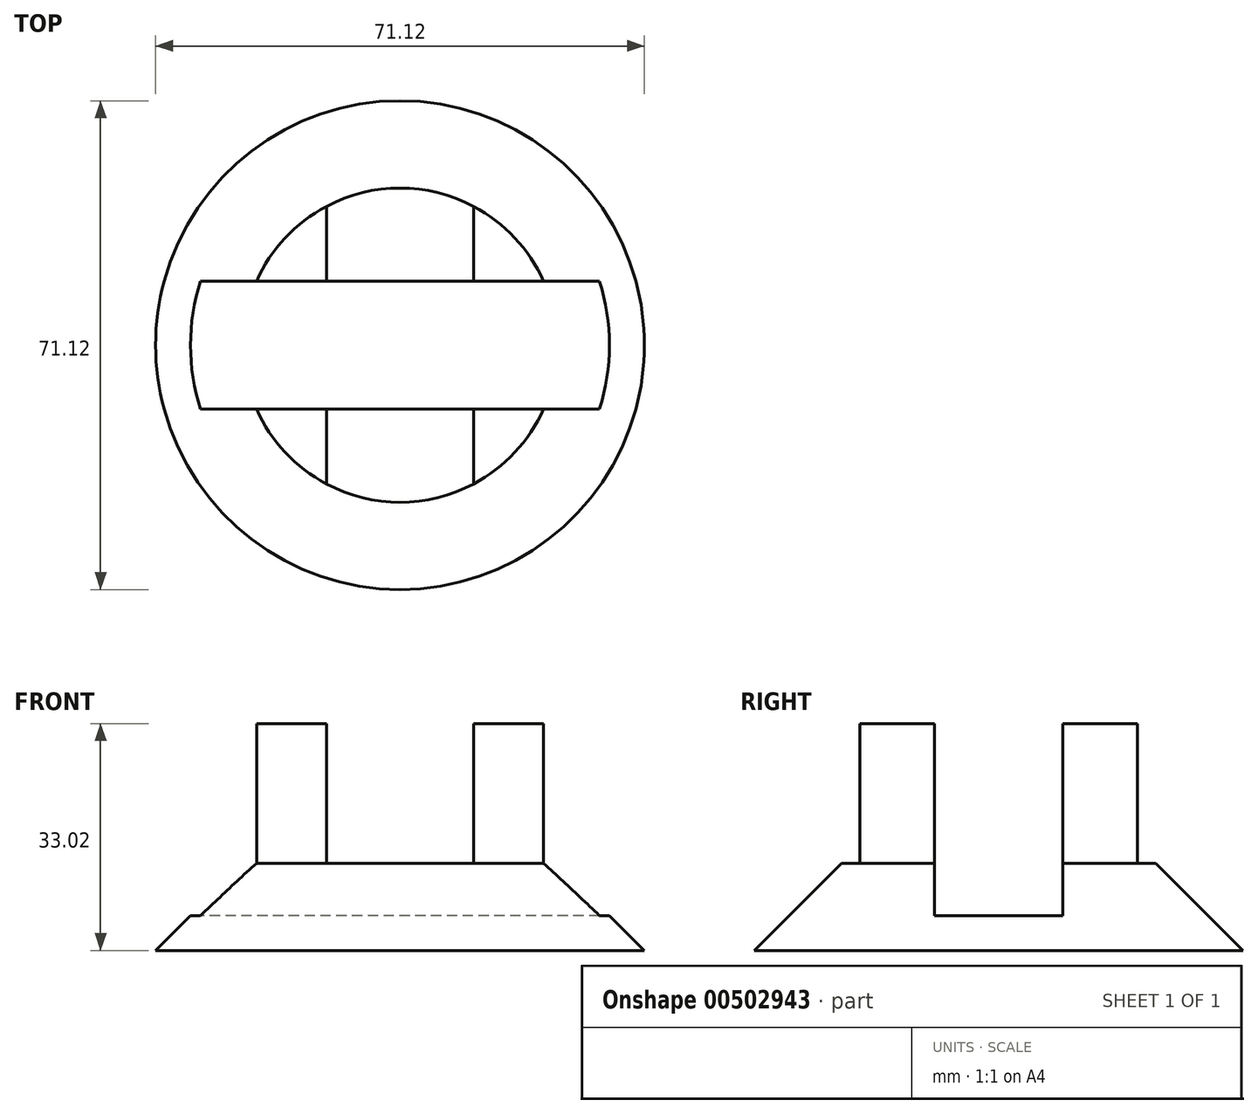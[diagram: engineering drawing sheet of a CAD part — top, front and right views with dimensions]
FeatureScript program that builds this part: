
annotation { "Feature Type Name" : "Feature", "Feature Type Description" : "" }
export const myFeature = defineFeature(function(context is Context, id is Id, definition is map)
    precondition{}
    {
        {
            var Q0;
            Q0=qCreatedBy(makeId("Top.planeOp"),FACE);
            var sketch = newSketch(context, id + "F0", { "sketchPlane" : qUnion([Q0])});
            skCircle(sketch, "E0", {"center": v(0, 0) * mm, "radius": 35.56 * mm});
            skLineSegment(sketch, "E1", {"start": v(34.32, -9.32) * mm, "end": v(-34.32, -9.32) * mm});
            skLineSegment(sketch, "E2", {"start": v(34.32, 9.32) * mm, "end": v(-34.32, 9.32) * mm});
            skSolve(sketch);
        }
        {
            var Q0;
            {var subQ2=sQuery(id+"F0.wireOp",EDGE,"E1");Q0=makeQuery(id+"F0.imprint","IMPRINT",FACE,{"disambiguationData":[TD([[makeQuery(id+"F0.imprint","IMPRINT",EDGE,{"derivedFrom":subQ2}),-1.0]])]});}
            extrude(context, id + "F1", {"entities" : qUnion([Q0]), "depth" : 5.08 * mm, "offsetDistance" : 25.4 * mm});
        }
        {
            var Q0;
            {var subQ0=sQuery(id+"F0.wireOp",EDGE,"E0");var subQ1=makeQuery(id+"F0.imprint","IMPRINT",VERTEX,{"derivedFrom":subQ0});Q0=makeQuery(id+"F1.opExtrude","CAP_EDGE",EDGE,{"disambiguationData":[OSD([subQ0]),TDD([makeQuery(id+"F0.imprint","IMPRINT",EDGE,{"disambiguationData":[TD([[subQ1,-1.0]])],"derivedFrom":subQ0}),makeQuery(id+"F0.imprint","IMPRINT",EDGE,{"disambiguationData":[TD([[subQ1,1.0]])],"derivedFrom":subQ0})])],"isStart":false});}
            var Q1;
            {var subQ0=sQuery(id+"F0.wireOp",EDGE,"E0");Q1=makeQuery(id+"F1.opExtrude","CAP_EDGE",EDGE,{"disambiguationData":[OSD([subQ0]),TDD([makeQuery(id+"F0.imprint","IMPRINT",EDGE,{"disambiguationData":[TD([[makeQuery(id+"F0.imprint","INTERSECT",VERTEX,{"disambiguationData":[OD(1.0)],"derivedFrom":[subQ0,sQuery(id+"F0.wireOp",EDGE,"E1")]}),1.0]])],"derivedFrom":subQ0})])],"isStart":false});}
            var Q2;
            {var subQ0=sQuery(id+"F0.wireOp",EDGE,"E0");Q2=makeQuery(id+"F1.opExtrude","CAP_EDGE",EDGE,{"disambiguationData":[OSD([subQ0]),TDD([makeQuery(id+"F0.imprint","IMPRINT",EDGE,{"disambiguationData":[TD([[makeQuery(id+"F0.imprint","INTERSECT",VERTEX,{"disambiguationData":[OD(0.0)],"derivedFrom":[subQ0,sQuery(id+"F0.wireOp",EDGE,"E1")]}),-1.0]])],"derivedFrom":subQ0})])],"isStart":false});}
            chamfer(context, id + "F2", {"entities" : qUnion([Q0, Q1, Q2]), "width" : 5.08 * mm, "tangentPropagation" : true});
        }
        {
            var Q0;
            {var subQ0=sQuery(id+"F0.wireOp",EDGE,"E1");Q0=makeQuery(id+"F0.imprint","IMPRINT",FACE,{"disambiguationData":[TD([[makeQuery(id+"F0.imprint","IMPRINT",EDGE,{"derivedFrom":subQ0}),1.0]])]});}
            extrude(context, id + "F3", {"entities" : qUnion([Q0]), "operationType" : NewBodyOperationType.ADD, "depth" : 12.7 * mm, "offsetDistance" : 25.4 * mm});
        }
        {
            var Q0;
            {var subQ0=sQuery(id+"F0.wireOp",EDGE,"E2");Q0=makeQuery(id+"F0.imprint","IMPRINT",FACE,{"disambiguationData":[TD([[makeQuery(id+"F0.imprint","IMPRINT",EDGE,{"derivedFrom":subQ0}),-1.0]])]});}
            extrude(context, id + "F4", {"entities" : qUnion([Q0]), "operationType" : NewBodyOperationType.ADD, "depth" : 12.7 * mm, "offsetDistance" : 25.4 * mm});
        }
        {
            var Q0;
            Q0=makeQuery(id+"F3.opExtrude","CAP_EDGE",EDGE,{"disambiguationData":[OSD([sQuery(id+"F0.wireOp",EDGE,"E0")])],"isStart":false});
            var Q1;
            Q1=makeQuery(id+"F4.opExtrude","CAP_EDGE",EDGE,{"disambiguationData":[OSD([sQuery(id+"F0.wireOp",EDGE,"E0")])],"isStart":false});
            chamfer(context, id + "F5", {"entities" : qUnion([Q0, Q1]), "width" : 12.7 * mm, "tangentPropagation" : true});
        }
        {
            var Q0;
            Q0=makeQuery(id+"F3.opExtrude","CAP_FACE",FACE,{"disambiguationData":[OSD([sQuery(id+"F0.wireOp",EDGE,"E0"),sQuery(id+"F0.wireOp",EDGE,"E1")])],"isStart":false});
            var sketch = newSketch(context, id + "F6", { "sketchPlane" : qUnion([Q0])});
            skLineSegment(sketch, "E3", {"start": v(20.87, -9.32) * mm, "end": v(10.71, -9.32) * mm});
            skLineSegment(sketch, "E4", {"start": v(-20.87, -9.32) * mm, "end": v(-10.71, -9.32) * mm});
            skLineSegment(sketch, "E5", {"start": v(-10.71, -9.32) * mm, "end": v(-10.71, -20.2) * mm});
            skLineSegment(sketch, "E6", {"start": v(10.71, -9.32) * mm, "end": v(10.71, -20.2) * mm});
            skSolve(sketch);
        }
        {
            var Q0;
            Q0=makeQuery(id+"F4.opExtrude","CAP_FACE",FACE,{"disambiguationData":[OSD([sQuery(id+"F0.wireOp",EDGE,"E0"),sQuery(id+"F0.wireOp",EDGE,"E2")])],"isStart":false});
            var sketch = newSketch(context, id + "F7", { "sketchPlane" : qUnion([Q0])});
            skLineSegment(sketch, "E7", {"start": v(20.87, 9.32) * mm, "end": v(10.71, 9.32) * mm});
            skLineSegment(sketch, "E8", {"start": v(-20.87, 9.32) * mm, "end": v(-10.71, 9.32) * mm});
            skLineSegment(sketch, "E9", {"start": v(-10.71, 9.32) * mm, "end": v(-10.71, 20.2) * mm});
            skLineSegment(sketch, "E10", {"start": v(10.71, 9.32) * mm, "end": v(10.71, 20.2) * mm});
            skSolve(sketch);
        }
        {
            var Q0;
            {var subQ0=sQuery(id+"F6.wireOp",EDGE,"E4");Q0=makeQuery(id+"F6.imprint","IMPRINT",FACE,{"disambiguationData":[TD([[makeQuery(id+"F6.imprint","IMPRINT",EDGE,{"derivedFrom":subQ0}),1.0]])]});}
            var Q1;
            {var subQ0=sQuery(id+"F6.wireOp",EDGE,"E3");Q1=makeQuery(id+"F6.imprint","IMPRINT",FACE,{"disambiguationData":[TD([[makeQuery(id+"F6.imprint","IMPRINT",EDGE,{"derivedFrom":subQ0}),1.0]])]});}
            extrude(context, id + "F8", {"entities" : qUnion([Q0, Q1]), "operationType" : NewBodyOperationType.ADD, "depth" : 20.32 * mm, "offsetDistance" : 25.4 * mm});
        }
        {
            var Q0;
            {var subQ0=sQuery(id+"F7.wireOp",EDGE,"E7");Q0=makeQuery(id+"F7.imprint","IMPRINT",FACE,{"disambiguationData":[TD([[makeQuery(id+"F7.imprint","IMPRINT",EDGE,{"derivedFrom":subQ0}),-1.0]])]});}
            var Q1;
            {var subQ0=sQuery(id+"F7.wireOp",EDGE,"E8");Q1=makeQuery(id+"F7.imprint","IMPRINT",FACE,{"disambiguationData":[TD([[makeQuery(id+"F7.imprint","IMPRINT",EDGE,{"derivedFrom":subQ0}),-1.0]])]});}
            extrude(context, id + "F9", {"entities" : qUnion([Q0, Q1]), "operationType" : NewBodyOperationType.ADD, "depth" : 20.32 * mm, "offsetDistance" : 25.4 * mm});
        }
    });
